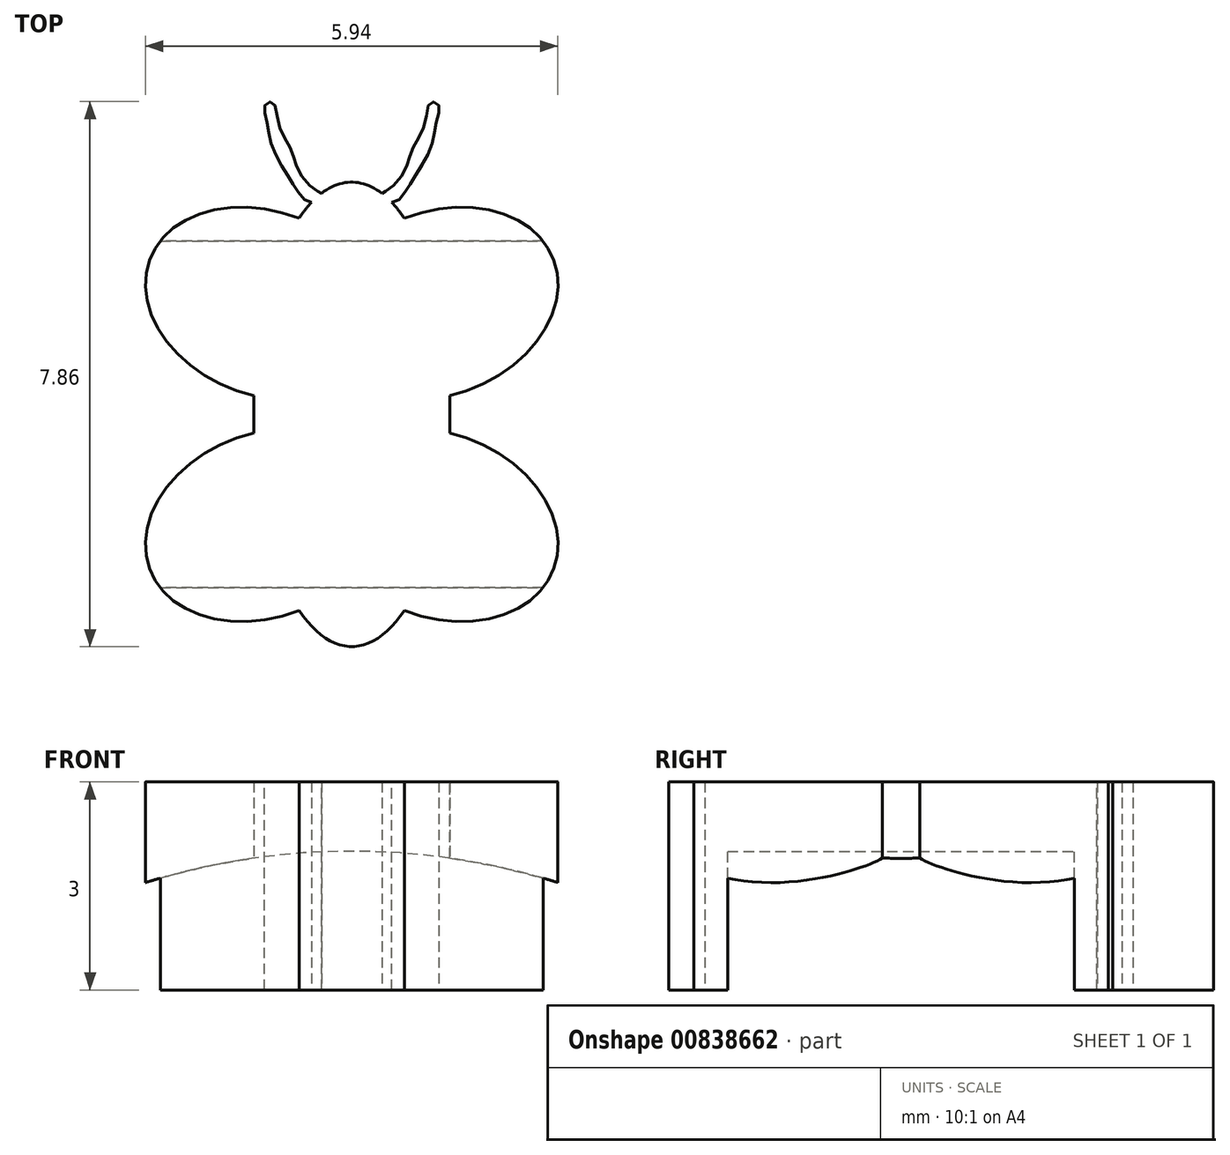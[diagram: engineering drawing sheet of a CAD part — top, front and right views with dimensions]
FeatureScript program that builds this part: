
annotation { "Feature Type Name" : "Feature", "Feature Type Description" : "" }
export const myFeature = defineFeature(function(context is Context, id is Id, definition is map)
    precondition{}
    {
        {
            var Q0;
            Q0=qCreatedBy(makeId("Top.planeOp"),FACE);
            var sketch = newSketch(context, id + "F0", { "sketchPlane" : qUnion([Q0])});
            skEllipticalArc(sketch, "E0", {});
            skEllipticalArc(sketch, "E1.MirrorCS", {});
            skEllipticalArc(sketch, "E2.MirrorCS", {});
            skEllipticalArc(sketch, "E3.MirrorCS", {});
            skEllipticalArc(sketch, "E4.trimOffspring", {});
            skEllipticalArc(sketch, "E5.trimOffspring", {});
            skEllipticalArc(sketch, "E6.trimOffspring", {});
            skFitSpline(sketch, "E7", {"points": [v(-0.58, 3.06) * mm, v(-0.76, 3.2) * mm, v(-0.93, 3.45) * mm, v(-1.15, 3.88) * mm, v(-1.23, 4.24) * mm, v(-1.25, 4.46) * mm, v(-1.14, 4.5) * mm, v(-1.05, 4.18) * mm, v(-0.88, 3.83) * mm, v(-0.76, 3.5) * mm, v(-0.5, 3.22) * mm, v(-0.43, 3.19) * mm, v(-0.58, 3.06) * mm]});
            skEllipticalArc(sketch, "E8.trimOffspring", {});
            skFitSpline(sketch, "E9.MirrorCS", {"points": [v(0.58, 3.06) * mm, v(0.76, 3.2) * mm, v(0.93, 3.45) * mm, v(1.15, 3.88) * mm, v(1.23, 4.24) * mm, v(1.25, 4.46) * mm, v(1.14, 4.5) * mm, v(1.05, 4.18) * mm, v(0.88, 3.83) * mm, v(0.76, 3.5) * mm, v(0.5, 3.22) * mm, v(0.43, 3.19) * mm, v(0.58, 3.06) * mm]});
            skEllipticalArc(sketch, "E10.trimOffspring", {});
            skLineSegment(sketch, "E11", {"start": v(-1.41, 0.27) * mm, "end": v(-1.41, -0.27) * mm});
            const initialGuessF0  = {"E0": [-0.0012453802001065732, 0.0015976992990520196, 0.9325561588214851, -0.3610249446286461, 0.001782486492121862, 0.0013222124561705843, 1.5654655575184915, 4.895212768906863], "E1.MirrorCS": [-0.0012453802001065732, -0.0015976992990520196, 0.9325561588214851, 0.3610249446286461, 0.001782486492121862, 0.0013222124561705843, 1.3879725382727228, 4.717719749661095], "E2.MirrorCS": [0.0012453802001065732, 0.0015976992990520196, -0.9325561588214851, -0.3610249446286461, 0.001782486492121862, 0.0013222124561705843, 1.3879725382727228, 4.717719749661095], "E3.MirrorCS": [0.0012453802001065732, -0.0015976992990520196, -0.9325561588214851, 0.3610249446286461, 0.001782486492121862, 0.0013222124561705843, 1.5654655575184915, 4.895212768906863], "E4.trimOffspring": [0, 0, 0, -1, 0.003348290454596281, 0.001417118313054923, 5.717828826922512, 0.5653564802570746], "E5.trimOffspring": [0, 0, 0, -1, 0.003348290454596281, 0.001417118313054923, 1.490605466709848, 1.6509871868799453], "E6.trimOffspring": [0, 0, 0, -1, 0.003348290454596281, 0.001417118313054923, 2.576236173332719, 2.7206975702169363], "E8.trimOffspring": [0, 0, 0, -1, 0.003348290454596281, 0.001417118313054923, 3.5624877369626504, 3.706949133846867], "E10.trimOffspring": [0, 0, 0, -1, 0.003348290454596281, 0.001417118313054923, 2.8301917589993564, 3.4529935481802285]};
            skSetInitialGuess(sketch, initialGuessF0);
            skSolve(sketch);
        }
        {
            var Q0;
            Q0 = qSketchRegion(id + "F0", true);
            extrude(context, id + "F1", {"entities" : qUnion([Q0]), "depth" : 3 * mm, "offsetDistance" : 25 * mm});
        }
        {
            var Q0;
            Q0=qCreatedBy(makeId("Front.planeOp"),FACE);
            var sketch = newSketch(context, id + "F2", { "sketchPlane" : qUnion([Q0])});
            skLineSegment(sketch, "E12", {"start": v(0, 0) * mm, "end": v(0, -8) * mm, "construction": true});
            skCircle(sketch, "E13", {"center": v(0, -8) * mm, "radius": 10 * mm});
            skSolve(sketch);
        }
        {
            var Q0;
            Q0 = qSketchRegion(id + "F2", true);
            extrude(context, id + "F3", {"entities" : qUnion([Q0]), "operationType" : NewBodyOperationType.REMOVE, "endBound" : BoundingType.SYMMETRIC, "depth" : 5 * mm, "offsetDistance" : 25 * mm});
        }
    });
